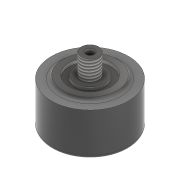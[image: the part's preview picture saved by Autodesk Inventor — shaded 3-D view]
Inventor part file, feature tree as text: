
AUTODESK INVENTOR PART (.ipt)
format: ipt  version: 2022.3 (Build 263350000, 350)  size: 218,624 bytes
history: native  units: mm
features: extrude x5, sketch x5, fillet x2, other x1, thread x1
ambient origin geometry x8: Origin, YZ Plane, XZ Plane, XY Plane, X Axis, Y Axis, Z Axis, Center Point
bodies: Body1 (feature_tree)
feature tree (14):
  other  "Sólido1"
  extrude  "Extrusión1"  Depth=23.25mm TaperAngle=0.0deg
  fillet  "Empalme1"  Radius=2.0mm
  extrude  "Extrusión2"  Depth=1.7mm TaperAngle=0.0deg
  extrude  "Extrusión3"  Depth=16.0mm
  extrude  "Extrusión4"  Depth=9.6mm
  thread  "Rosca1"  [1 undecoded]
  fillet  "Empalme2"  Radius=10.8mm
  extrude  "Extrusión5"  Depth=2.0mm
  sketch  "Boceto1"  dims[d0=41.85mm d1=23.25mm d2=0.0mm d3=2.0mm]
  sketch  "Boceto2"  dims[d4=29.5mm d5=1.7mm d6=0.0mm]
  sketch  "Boceto3"  dims[d7=22.5mm d8=16.0mm]
  sketch  "Boceto4"  dims[d9=1.7mm d10=0.0mm d11=9.6mm d12=4.7mm d13=10.8mm d14=0.0mm]
  sketch  "Boceto5"  dims[d15=10.8mm d16=0.0mm d17=2.0mm d27=1.0mm d28=0.0mm]
note: 1 required parameter value undecoded (feature->parameter linkage not recoverable at this tier; creation-order binding heuristic only, values carry confidence <= 0.55)
